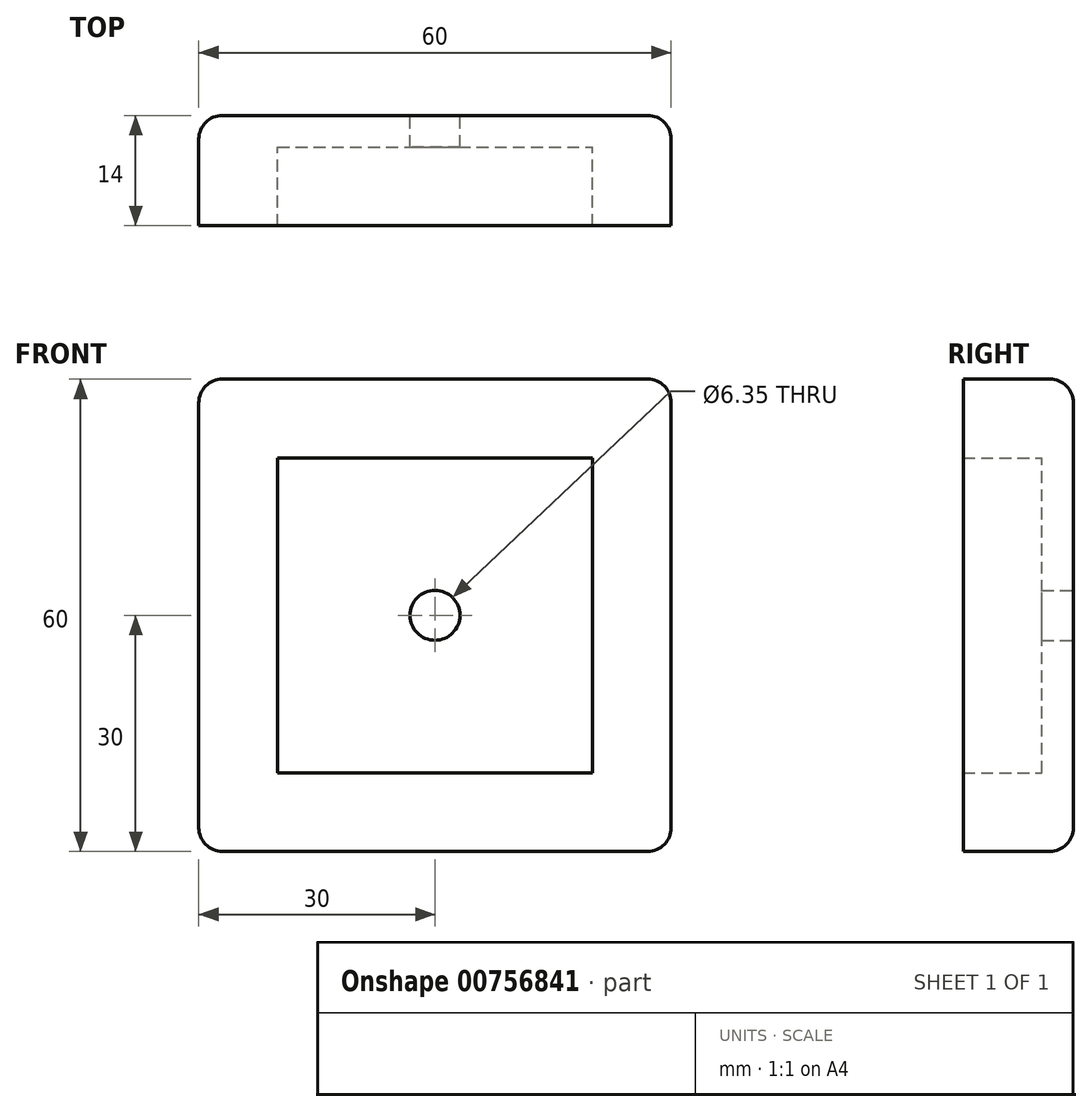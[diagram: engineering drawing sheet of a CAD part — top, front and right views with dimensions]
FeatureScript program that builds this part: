
annotation { "Feature Type Name" : "Feature", "Feature Type Description" : "" }
export const myFeature = defineFeature(function(context is Context, id is Id, definition is map)
    precondition{}
    {
        {
            var Q0;
            Q0=qCreatedBy(makeId("Front.planeOp"),FACE);
            var sketch = newSketch(context, id + "F0", { "sketchPlane" : qUnion([Q0])});
            skLineSegment(sketch, "E0.bottom", {"start": v(0, 0) * mm, "end": v(60, 0) * mm});
            skLineSegment(sketch, "E0.top", {"start": v(0, 60) * mm, "end": v(60, 60) * mm});
            skLineSegment(sketch, "E0.left", {"start": v(0, 0) * mm, "end": v(0, 60) * mm});
            skLineSegment(sketch, "E0.right", {"start": v(60, 0) * mm, "end": v(60, 60) * mm});
            skLineSegment(sketch, "E1.0", {"start": v(30, 0) * mm, "end": v(30, 60) * mm, "construction": true});
            skLineSegment(sketch, "E2.0", {"start": v(0, 30) * mm, "end": v(45, 30) * mm, "construction": true});
            skCircle(sketch, "E3", {"center": v(30, 30) * mm, "radius": 3.17 * mm});
            skLineSegment(sketch, "E4.0", {"start": v(10, 50) * mm, "end": v(50, 50) * mm});
            skLineSegment(sketch, "E5.0", {"start": v(10, 10) * mm, "end": v(50, 10) * mm});
            skLineSegment(sketch, "E6.0", {"start": v(50, 10) * mm, "end": v(50, 50) * mm});
            skLineSegment(sketch, "E7.0", {"start": v(10, 10) * mm, "end": v(10, 50) * mm});
            skSolve(sketch);
        }
        {
            var Q0;
            {var subQ0=sQuery(id+"F0.wireOp",EDGE,"E4.0");var subQ1=sQuery(id+"F0.wireOp",EDGE,"E0.left");var subQ2=makeQuery(id+"F0.imprint","INTERSECT",VERTEX,{"derivedFrom":[subQ1,subQ0]});Q0=makeQuery(id+"F0.imprint","IMPRINT",FACE,{"disambiguationData":[TD([[makeQuery(id+"F0.imprint","IMPRINT",EDGE,{"disambiguationData":[TD([[subQ2,1.0]])],"derivedFrom":subQ1}),-1.0]])]});}
            var Q1;
            {var subQ0=sQuery(id+"F0.wireOp",EDGE,"E0.left");var subQ1=sQuery(id+"F0.wireOp",EDGE,"E0.top");var subQ2=makeQuery(id+"F0.imprint","INTERSECT",VERTEX,{"derivedFrom":[subQ1,subQ0]});Q1=makeQuery(id+"F0.imprint","IMPRINT",FACE,{"disambiguationData":[TD([[makeQuery(id+"F0.imprint","IMPRINT",EDGE,{"disambiguationData":[TD([[subQ2,-1.0]])],"derivedFrom":subQ1}),-1.0]])]});}
            var Q2;
            {var subQ0=sQuery(id+"F0.wireOp",EDGE,"E6.0");var subQ1=sQuery(id+"F0.wireOp",EDGE,"E0.top");var subQ2=makeQuery(id+"F0.imprint","INTERSECT",VERTEX,{"derivedFrom":[subQ1,subQ0]});Q2=makeQuery(id+"F0.imprint","IMPRINT",FACE,{"disambiguationData":[TD([[makeQuery(id+"F0.imprint","IMPRINT",EDGE,{"disambiguationData":[TD([[subQ2,1.0]])],"derivedFrom":subQ1}),-1.0]])]});}
            var Q3;
            {var subQ0=sQuery(id+"F0.wireOp",EDGE,"E0.right");var subQ1=sQuery(id+"F0.wireOp",EDGE,"E0.top");var subQ2=makeQuery(id+"F0.imprint","INTERSECT",VERTEX,{"derivedFrom":[subQ1,subQ0]});Q3=makeQuery(id+"F0.imprint","IMPRINT",FACE,{"disambiguationData":[TD([[makeQuery(id+"F0.imprint","IMPRINT",EDGE,{"disambiguationData":[TD([[subQ2,1.0]])],"derivedFrom":subQ1}),-1.0]])]});}
            var Q4;
            {var subQ0=sQuery(id+"F0.wireOp",EDGE,"E4.0");var subQ1=sQuery(id+"F0.wireOp",EDGE,"E0.right");var subQ2=makeQuery(id+"F0.imprint","INTERSECT",VERTEX,{"derivedFrom":[subQ1,subQ0]});Q4=makeQuery(id+"F0.imprint","IMPRINT",FACE,{"disambiguationData":[TD([[makeQuery(id+"F0.imprint","IMPRINT",EDGE,{"disambiguationData":[TD([[subQ2,1.0]])],"derivedFrom":subQ1}),1.0]])]});}
            var Q5;
            {var subQ0=sQuery(id+"F0.wireOp",EDGE,"E0.right");var subQ1=sQuery(id+"F0.wireOp",EDGE,"E0.bottom");var subQ2=makeQuery(id+"F0.imprint","INTERSECT",VERTEX,{"derivedFrom":[subQ1,subQ0]});Q5=makeQuery(id+"F0.imprint","IMPRINT",FACE,{"disambiguationData":[TD([[makeQuery(id+"F0.imprint","IMPRINT",EDGE,{"disambiguationData":[TD([[subQ2,1.0]])],"derivedFrom":subQ1}),1.0]])]});}
            var Q6;
            {var subQ0=sQuery(id+"F0.wireOp",EDGE,"E6.0");var subQ1=sQuery(id+"F0.wireOp",EDGE,"E0.bottom");var subQ2=makeQuery(id+"F0.imprint","INTERSECT",VERTEX,{"derivedFrom":[subQ1,subQ0]});Q6=makeQuery(id+"F0.imprint","IMPRINT",FACE,{"disambiguationData":[TD([[makeQuery(id+"F0.imprint","IMPRINT",EDGE,{"disambiguationData":[TD([[subQ2,1.0]])],"derivedFrom":subQ1}),1.0]])]});}
            var Q7;
            {var subQ0=sQuery(id+"F0.wireOp",EDGE,"E0.left");var subQ1=sQuery(id+"F0.wireOp",EDGE,"E0.bottom");var subQ2=makeQuery(id+"F0.imprint","INTERSECT",VERTEX,{"derivedFrom":[subQ1,subQ0]});Q7=makeQuery(id+"F0.imprint","IMPRINT",FACE,{"disambiguationData":[TD([[makeQuery(id+"F0.imprint","IMPRINT",EDGE,{"disambiguationData":[TD([[subQ2,-1.0]])],"derivedFrom":subQ1}),1.0]])]});}
            extrude(context, id + "F1", {"entities" : qUnion([Q0, Q1, Q2, Q3, Q4, Q5, Q6, Q7]), "depth" : 14 * mm, "offsetDistance" : 25 * mm});
        }
        {
            var Q0;
            Q0=makeQuery(id+"F0.imprint","IMPRINT",FACE,{"disambiguationData":[TD([[makeQuery(id+"F0.imprint","IMPRINT",EDGE,{"derivedFrom":sQuery(id+"F0.wireOp",EDGE,"E3")}),-1.0]])]});
            extrude(context, id + "F2", {"entities" : qUnion([Q0]), "operationType" : NewBodyOperationType.ADD, "depth" : 4 * mm, "offsetDistance" : 25 * mm});
        }
        {
            var Q0;
            Q0=makeQuery(id+"F1.opExtrude","SWEPT_EDGE",EDGE,{"disambiguationData":[OSD([sQuery(id+"F0.wireOp",EDGE,"E0.bottom"),sQuery(id+"F0.wireOp",EDGE,"E0.left")])]});
            var Q1;
            Q1=makeQuery(id+"F1.opExtrude","SWEPT_EDGE",EDGE,{"disambiguationData":[OSD([sQuery(id+"F0.wireOp",EDGE,"E0.top"),sQuery(id+"F0.wireOp",EDGE,"E0.left")])]});
            var Q2;
            Q2=makeQuery(id+"F1.opExtrude","SWEPT_EDGE",EDGE,{"disambiguationData":[OSD([sQuery(id+"F0.wireOp",EDGE,"E0.top"),sQuery(id+"F0.wireOp",EDGE,"E0.right")])]});
            var Q3;
            Q3=makeQuery(id+"F1.opExtrude","SWEPT_EDGE",EDGE,{"disambiguationData":[OSD([sQuery(id+"F0.wireOp",EDGE,"E0.bottom"),sQuery(id+"F0.wireOp",EDGE,"E0.right")])]});
            var Q4;
            Q4=makeQuery(id+"F1.opExtrude","CAP_EDGE",EDGE,{"disambiguationData":[OSD([sQuery(id+"F0.wireOp",EDGE,"E0.right")])],"isStart":true});
            var Q5;
            Q5=makeQuery(id+"F1.opExtrude","CAP_EDGE",EDGE,{"disambiguationData":[OSD([sQuery(id+"F0.wireOp",EDGE,"E0.top")])],"isStart":true});
            var Q6;
            Q6=makeQuery(id+"F1.opExtrude","CAP_EDGE",EDGE,{"disambiguationData":[OSD([sQuery(id+"F0.wireOp",EDGE,"E0.left")])],"isStart":true});
            var Q7;
            Q7=makeQuery(id+"F1.opExtrude","CAP_EDGE",EDGE,{"disambiguationData":[OSD([sQuery(id+"F0.wireOp",EDGE,"E0.bottom")])],"isStart":true});
            fillet(context, id + "F3", {"entities" : qUnion([Q0, Q1, Q2, Q3, Q4, Q5, Q6, Q7]), "radius" : 3 * mm, "tangentPropagation" : true, "allowEdgeOverflow" : false});
        }
    });
